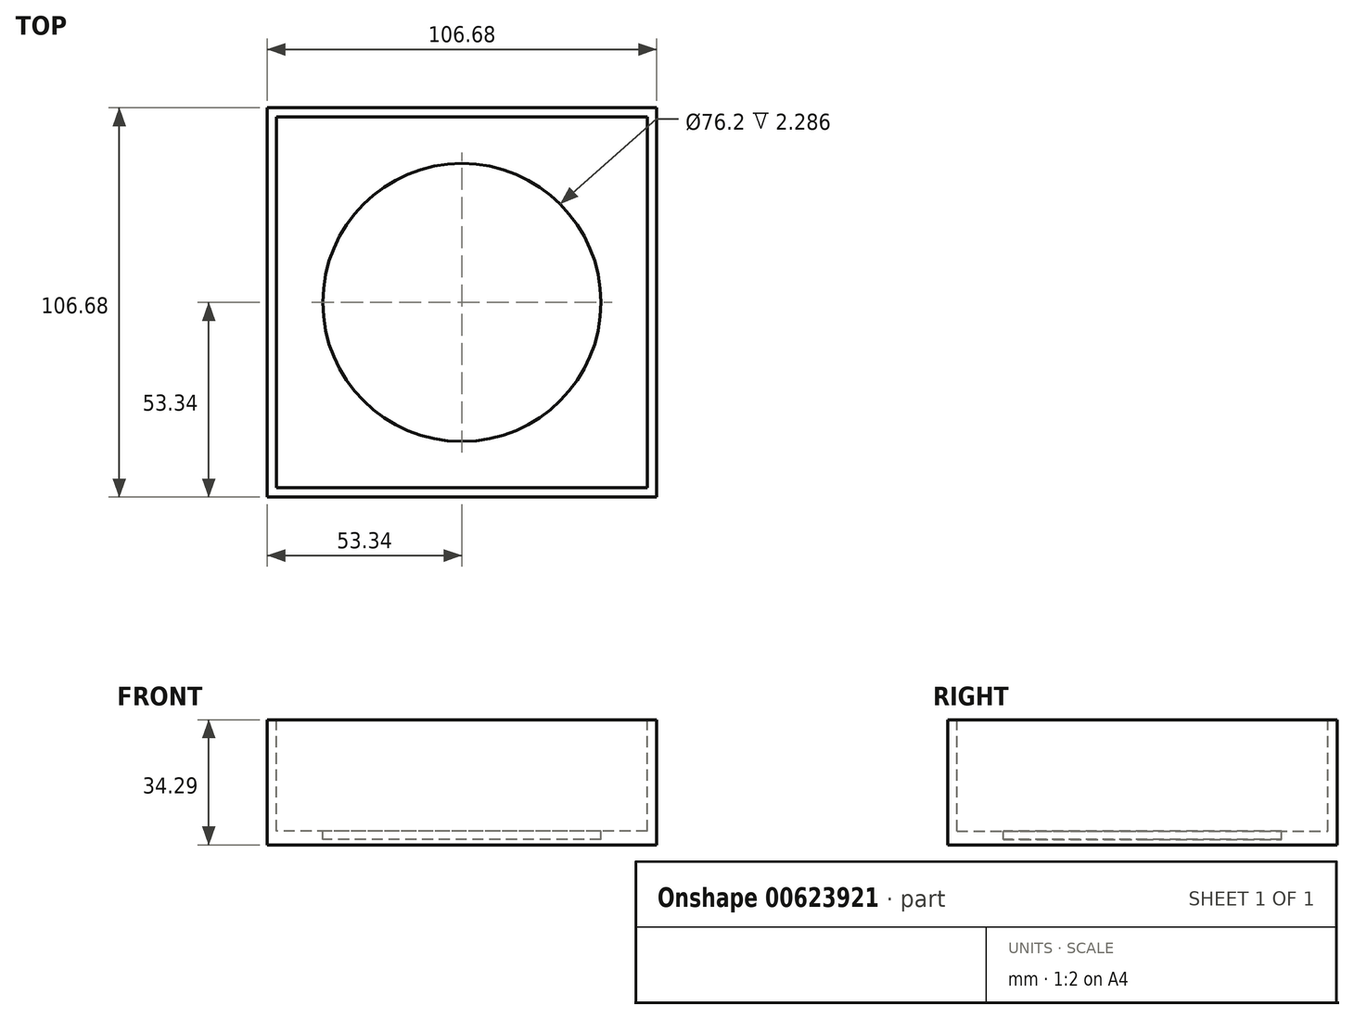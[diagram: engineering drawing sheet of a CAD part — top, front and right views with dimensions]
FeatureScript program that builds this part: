
annotation { "Feature Type Name" : "Feature", "Feature Type Description" : "" }
export const myFeature = defineFeature(function(context is Context, id is Id, definition is map)
    precondition{}
    {
        {
            var Q0;
            Q0=qCreatedBy(makeId("Top.planeOp"),FACE);
            var sketch = newSketch(context, id + "F0", { "sketchPlane" : qUnion([Q0])});
            skLineSegment(sketch, "E0.bottom", {"start": v(53.34, -53.34) * mm, "end": v(-53.34, -53.34) * mm});
            skLineSegment(sketch, "E0.top", {"start": v(53.34, 53.34) * mm, "end": v(-53.34, 53.34) * mm});
            skLineSegment(sketch, "E0.left", {"start": v(53.34, -53.34) * mm, "end": v(53.34, 53.34) * mm});
            skLineSegment(sketch, "E0.right", {"start": v(-53.34, -53.34) * mm, "end": v(-53.34, 53.34) * mm});
            skPoint(sketch, "E0.middle", {"position": v(0, 0) * mm});
            skLineSegment(sketch, "E1.bottom", {"start": v(50.8, -50.8) * mm, "end": v(-50.8, -50.8) * mm});
            skLineSegment(sketch, "E1.top", {"start": v(50.8, 50.8) * mm, "end": v(-50.8, 50.8) * mm});
            skLineSegment(sketch, "E1.left", {"start": v(50.8, -50.8) * mm, "end": v(50.8, 50.8) * mm});
            skLineSegment(sketch, "E1.right", {"start": v(-50.8, -50.8) * mm, "end": v(-50.8, 50.8) * mm});
            skCircle(sketch, "E2", {"center": v(0, 0) * mm, "radius": 38.1 * mm});
            skSolve(sketch);
        }
        {
            var Q0;
            Q0 = qSketchRegion(id + "F0", true);
            var Q1;
            Q1=makeQuery(id+"F0.imprint","IMPRINT",FACE,{"disambiguationData":[TD([[makeQuery(id+"F0.imprint","IMPRINT",EDGE,{"derivedFrom":sQuery(id+"F0.wireOp",EDGE,"E1.bottom")}),-1.0]])]});
            var Q2;
            Q2=makeQuery(id+"F0.imprint","IMPRINT",FACE,{"disambiguationData":[TD([[makeQuery(id+"F0.imprint","IMPRINT",EDGE,{"derivedFrom":sQuery(id+"F0.wireOp",EDGE,"E2")}),1.0]])]});
            extrude(context, id + "F1", {"entities" : qUnion([Q0, Q1, Q2]), "oppositeDirection" : true, "depth" : 8.9 * mm, "offsetDistance" : 25.4 * mm});
        }
        {
            var Q0;
            Q0=makeQuery(id+"F0.imprint","IMPRINT",FACE,{"disambiguationData":[TD([[makeQuery(id+"F0.imprint","IMPRINT",EDGE,{"derivedFrom":sQuery(id+"F0.wireOp",EDGE,"E1.bottom")}),-1.0]])]});
            extrude(context, id + "F2", {"entities" : qUnion([Q0]), "operationType" : NewBodyOperationType.REMOVE, "oppositeDirection" : true, "depth" : 5.08 * mm, "offsetDistance" : 25.4 * mm});
        }
        {
            var Q0;
            Q0=makeQuery(id+"F0.imprint","IMPRINT",FACE,{"disambiguationData":[TD([[makeQuery(id+"F0.imprint","IMPRINT",EDGE,{"derivedFrom":sQuery(id+"F0.wireOp",EDGE,"E2")}),1.0]])]});
            extrude(context, id + "F3", {"entities" : qUnion([Q0]), "operationType" : NewBodyOperationType.REMOVE, "oppositeDirection" : true, "depth" : 7.37 * mm, "offsetDistance" : 25.4 * mm});
        }
        {
            var Q0;
            {var subQ0=sQuery(id+"F0.wireOp",EDGE,"E0.left");var subQ1=sQuery(id+"F0.wireOp",EDGE,"E0.top");var subQ2=sQuery(id+"F0.wireOp",EDGE,"E0.right");var subQ3=sQuery(id+"F0.wireOp",EDGE,"E0.bottom");Q0=makeQuery(id+"F2.boolean.opBoolean","SPLIT",FACE,{"disambiguationData":[TD([makeQuery(id+"F1.opExtrude","SWEPT_FACE",FACE,{"disambiguationData":[OSD([subQ3])]})])],"derivedFrom":makeQuery(id+"F1.opExtrude","CAP_FACE",FACE,{"disambiguationData":[OSD([subQ3,subQ1,subQ0,subQ2])],"isStart":true})});}
            extrude(context, id + "F4", {"entities" : qUnion([Q0]), "operationType" : NewBodyOperationType.ADD, "depth" : 25.4 * mm, "offsetDistance" : 25.4 * mm});
        }
    });
